# Revit family: Flush_Valve-Toilet-American_Standard-Ultima_Manual-6147_Series
name_source: partatom
category: Plumbing Fixtures
revit_build: Autodesk Revit 2014 (Build: 20130308_1515(x64)
units: mm (PartAtom-declared; Revit-internal decimal feet)

## types (5) — shared parameters
ADA Compliant = Yes
Assembly Code = D2020300
CW Connection = Yes
CWFU = 10
Cold Water Connection Diameter = 1"
Cold Water Connection Radius = 1/2"
Cold Water Connection Width = 4 1/4"
Default Elevation = 0"
Description = Ultima Manual Toilet Flush Valve Diaphragm-Type
Finish = Brass-American Standard-002-Polished Chrome
HW Connection = No
Installation Type = Top Spud
Manufacturer = American Standard
Material = Brass-American Standard-002-Polished Chrome
Price = Prices may vary. Please consult Manufacturer Representative for most up-to-date price list.
URL = https://www.americanstandard-us.com
Vent Connection = No
Warranty Information = 1 Year Limited Warranty
Waste Connection = No
zero-valued in all types: HWFU, WFU

## per-type parameters (varying)
| type | Cold Water Connection Height | Flush Rate | Height | Model |
| 6147111.002 | 11 1/2" | 1.1 gpf (4.2 Lpf) | 14 5/8" | 6147111.002 |
| 6147121.002 | 11 1/2" | 1.28 gpf (4.8 Lpf) | 14 5/8" | 6147121.002 |
| 6147122.002 | 27" | 1.28 gpf (4.8 Lpf) | 30 1/8" | 6147122.002 |
| 6147161.002 | 11 1/2" | 1.6 gpf (6.0 Lpf) | 14 5/8" | 6147161.002 |
| 6147162.002 | 27" | 1.6 gpf (6.0 Lpf) | 30 1/8" | 6147122.002 |

## geometry (parser evidence)
native form markers: Sweep x1
no freeform markers — native parametric forms only
